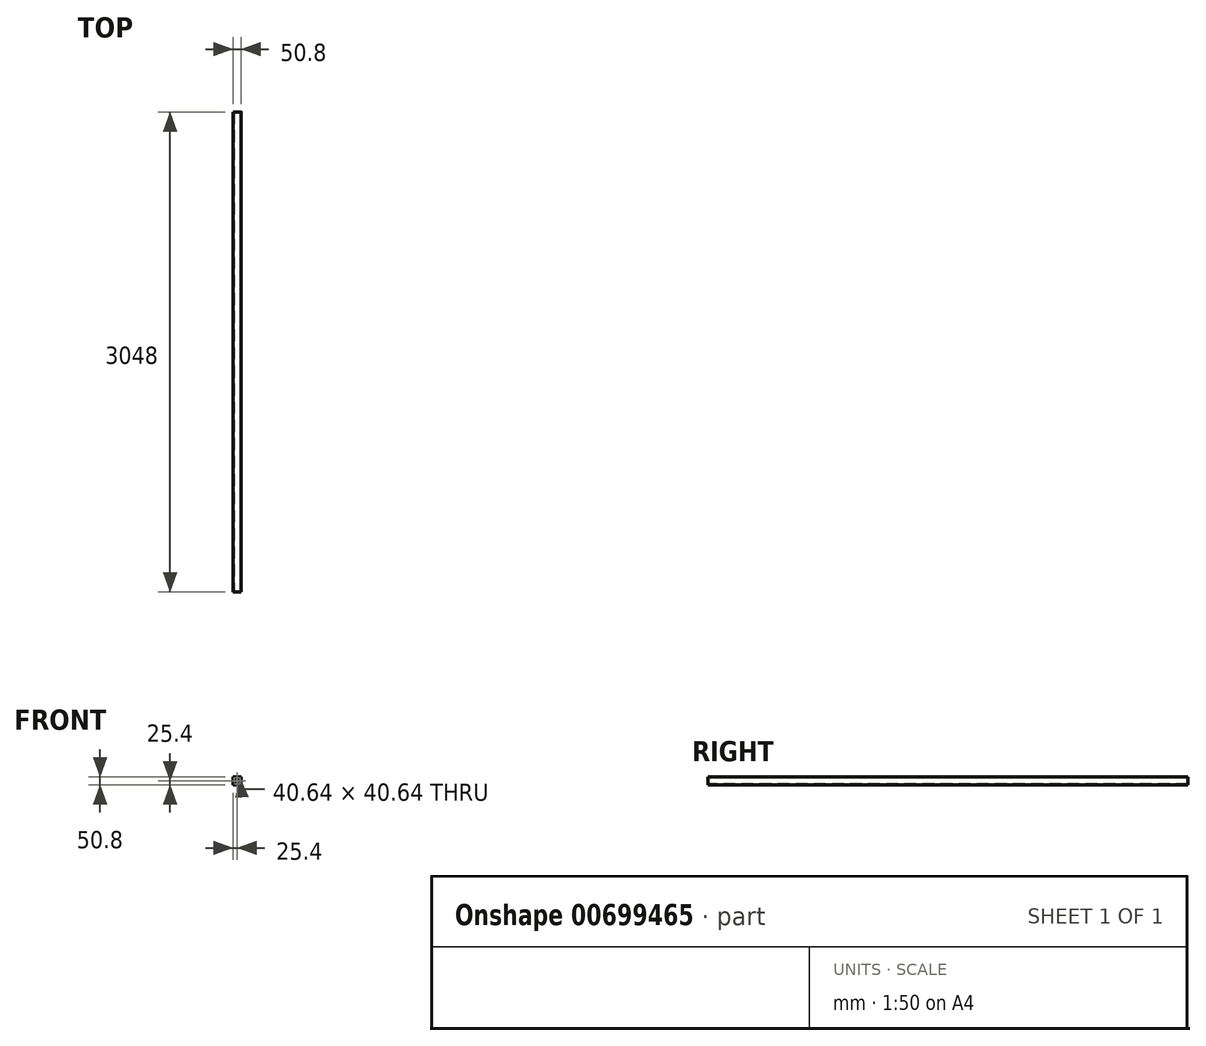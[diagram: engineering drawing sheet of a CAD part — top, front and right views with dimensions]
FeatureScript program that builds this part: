
annotation { "Feature Type Name" : "Feature", "Feature Type Description" : "" }
export const myFeature = defineFeature(function(context is Context, id is Id, definition is map)
    precondition{}
    {
        {
            var Q0;
            Q0=qCreatedBy(makeId("Front.planeOp"),FACE);
            var sketch = newSketch(context, id + "F0", { "sketchPlane" : qUnion([Q0])});
            skLineSegment(sketch, "E0.bottom", {"start": v(22.23, 25.4) * mm, "end": v(-22.23, 25.4) * mm});
            skLineSegment(sketch, "E0.top", {"start": v(22.23, -25.4) * mm, "end": v(-22.23, -25.4) * mm});
            skLineSegment(sketch, "E0.left", {"start": v(25.4, 22.23) * mm, "end": v(25.4, -22.23) * mm});
            skLineSegment(sketch, "E0.right", {"start": v(-25.4, 22.23) * mm, "end": v(-25.4, -22.22) * mm});
            skPoint(sketch, "E0.middle", {"position": v(0, 0) * mm});
            skPoint(sketch, "E1.visualSharp", {"position": v(-25.4, 25.4) * mm});
            skArc(sketch, "E1.filletArc", {"start": v(-22.23, 25.4) * mm, "mid": v(-24.47, 24.47) * mm, "end": v(-25.4, 22.23) * mm});
            skPoint(sketch, "E2.visualSharp", {"position": v(-25.4, -25.4) * mm});
            skArc(sketch, "E2.filletArc", {"start": v(-25.4, -22.22) * mm, "mid": v(-24.47, -24.47) * mm, "end": v(-22.23, -25.4) * mm});
            skPoint(sketch, "E3.visualSharp", {"position": v(25.4, -25.4) * mm});
            skArc(sketch, "E3.filletArc", {"start": v(22.23, -25.4) * mm, "mid": v(24.47, -24.47) * mm, "end": v(25.4, -22.23) * mm});
            skPoint(sketch, "E4.visualSharp", {"position": v(25.4, 25.4) * mm});
            skArc(sketch, "E4.filletArc", {"start": v(25.4, 22.23) * mm, "mid": v(24.47, 24.47) * mm, "end": v(22.23, 25.4) * mm});
            skLineSegment(sketch, "E5.0", {"start": v(20.32, 20.32) * mm, "end": v(-20.32, 20.32) * mm});
            skLineSegment(sketch, "E5.1", {"start": v(20.32, 20.32) * mm, "end": v(20.32, -20.32) * mm});
            skLineSegment(sketch, "E5.2", {"start": v(20.32, -20.32) * mm, "end": v(-20.32, -20.32) * mm});
            skLineSegment(sketch, "E5.3", {"start": v(-20.32, 20.32) * mm, "end": v(-20.32, -20.32) * mm});
            skSolve(sketch);
        }
        {
            var Q0;
            Q0 = qSketchRegion(id + "F0", true);
            extrude(context, id + "F1", {"entities" : qUnion([Q0]), "oppositeDirection" : true, "depth" : 3048 * mm, "offsetDistance" : 25.4 * mm});
        }
    });
